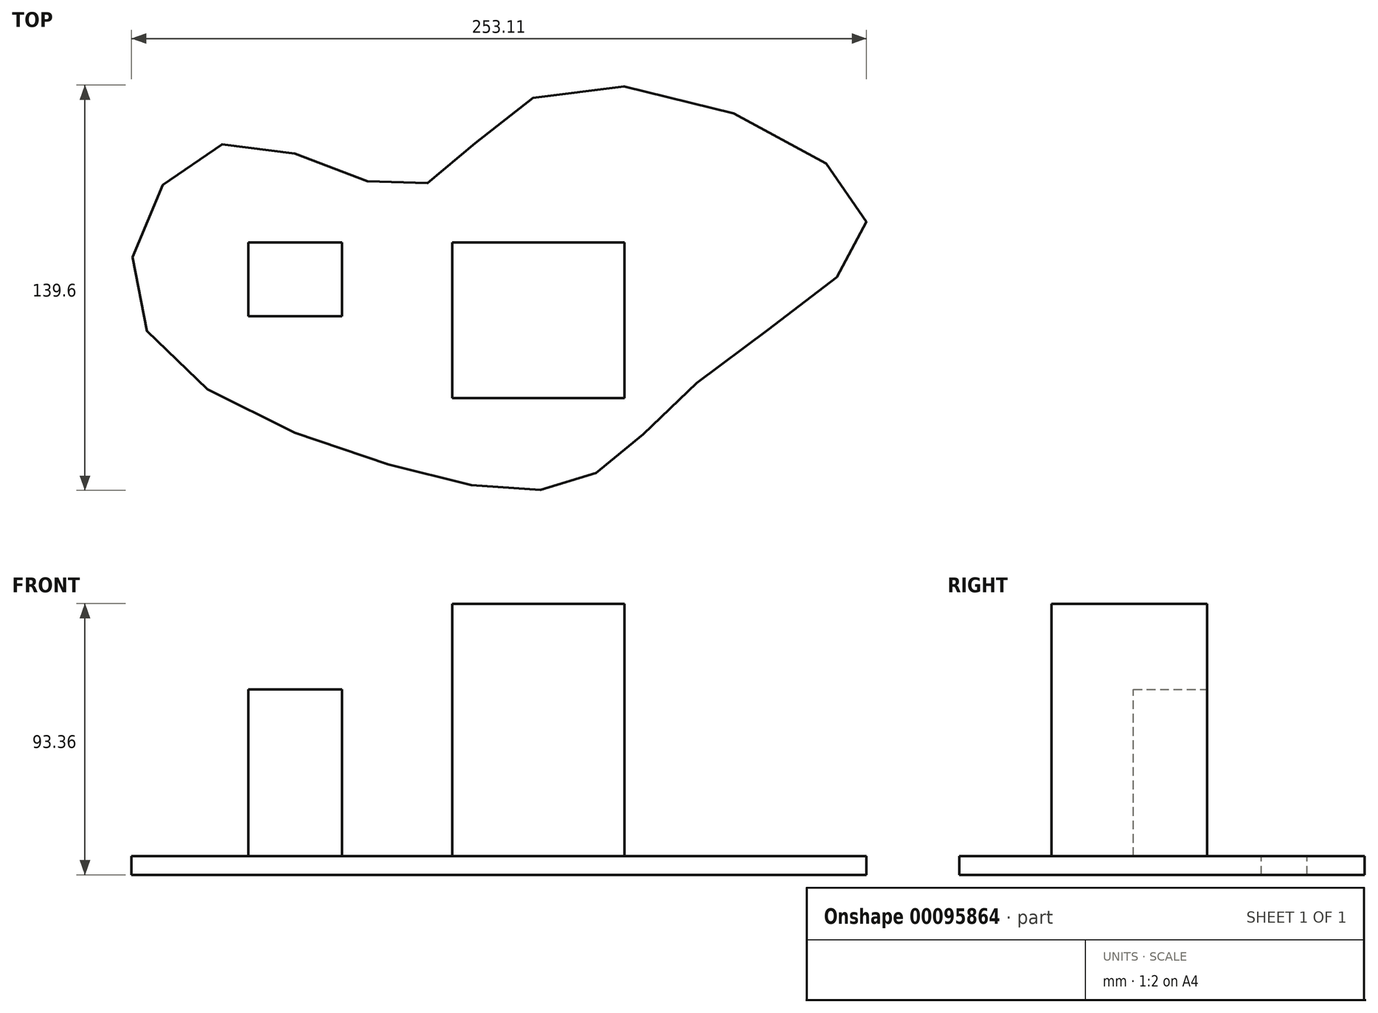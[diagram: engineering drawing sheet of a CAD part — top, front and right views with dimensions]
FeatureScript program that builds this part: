
annotation { "Feature Type Name" : "Feature", "Feature Type Description" : "" }
export const myFeature = defineFeature(function(context is Context, id is Id, definition is map)
    precondition{}
    {
        {
            var Q0;
            Q0=qCreatedBy(makeId("Front.planeOp"),FACE);
            var sketch = newSketch(context, id + "F0", { "sketchPlane" : qUnion([Q0])});
            skLineSegment(sketch, "E0.bottom", {"start": v(0, 0) * mm, "end": v(59.24, 0) * mm});
            skLineSegment(sketch, "E0.top", {"start": v(0, 86.9) * mm, "end": v(59.24, 86.9) * mm});
            skLineSegment(sketch, "E0.left", {"start": v(0, 0) * mm, "end": v(0, 86.9) * mm});
            skLineSegment(sketch, "E0.right", {"start": v(59.24, 0) * mm, "end": v(59.24, 86.9) * mm});
            skSolve(sketch);
        }
        {
            var Q0;
            Q0=makeQuery(id+"F0.imprint","IMPRINT",FACE,{"disambiguationData":[TD([[makeQuery(id+"F0.imprint","IMPRINT",EDGE,{"derivedFrom":sQuery(id+"F0.wireOp",EDGE,"E0.bottom")}),1.0]])]});
            extrude(context, id + "F1", {"entities" : qUnion([Q0]), "depth" : 53.6 * mm});
        }
        {
            var Q0;
            Q0=qCreatedBy(makeId("Front.planeOp"),FACE);
            var sketch = newSketch(context, id + "F2", { "sketchPlane" : qUnion([Q0])});
            skLineSegment(sketch, "E1.bottom", {"start": v(-37.98, 0) * mm, "end": v(-70.25, 0) * mm});
            skLineSegment(sketch, "E1.top", {"start": v(-37.98, 57.37) * mm, "end": v(-70.25, 57.37) * mm});
            skLineSegment(sketch, "E1.left", {"start": v(-37.98, 0) * mm, "end": v(-37.98, 57.37) * mm});
            skLineSegment(sketch, "E1.right", {"start": v(-70.25, 0) * mm, "end": v(-70.25, 57.37) * mm});
            skSolve(sketch);
        }
        {
            var Q0;
            Q0=makeQuery(id+"F2.imprint","IMPRINT",FACE,{"disambiguationData":[TD([[makeQuery(id+"F2.imprint","IMPRINT",EDGE,{"derivedFrom":sQuery(id+"F2.wireOp",EDGE,"E1.bottom")}),-1.0]])]});
            extrude(context, id + "F3", {"entities" : qUnion([Q0]), "depth" : 25.4 * mm});
        }
        {
            var Q0;
            Q0=makeQuery(id+"F1.opExtrude","SWEPT_FACE",FACE,{"disambiguationData":[OSD([sQuery(id+"F0.wireOp",EDGE,"E0.bottom")])]});
            var sketch = newSketch(context, id + "F4", { "sketchPlane" : qUnion([Q0])});
            skLineSegment(sketch, "E2.0.0", {"start": v(0, 0) * mm, "end": v(59.24, 0) * mm});
            skLineSegment(sketch, "E2.0.1", {"start": v(59.24, 0) * mm, "end": v(59.24, 53.59) * mm});
            skLineSegment(sketch, "E2.0.2", {"start": v(59.24, 53.59) * mm, "end": v(0, 53.59) * mm});
            skLineSegment(sketch, "E2.0.3", {"start": v(0, 53.59) * mm, "end": v(0, 0) * mm});
            skLineSegment(sketch, "E3.0.0", {"start": v(-70.25, 0) * mm, "end": v(-37.98, 0) * mm});
            skLineSegment(sketch, "E3.0.1", {"start": v(-37.98, 0) * mm, "end": v(-37.98, 25.4) * mm});
            skLineSegment(sketch, "E3.0.2", {"start": v(-37.98, 25.4) * mm, "end": v(-70.25, 25.4) * mm});
            skLineSegment(sketch, "E3.0.3", {"start": v(-70.25, 25.4) * mm, "end": v(-70.25, 0) * mm});
            skFitSpline(sketch, "E4", {"points": [v(-21.97, 76.37) * mm, v(44.35, 81.9) * mm, v(90.77, 42.94) * mm, v(142.17, -10.12) * mm, v(35.78, -52.67) * mm, v(-13.4, -18.96) * mm, v(-79.17, -33.88) * mm, v(-109.01, 21.66) * mm, v(-21.97, 76.37) * mm]});
            skSolve(sketch);
        }
        {
            var Q0;
            Q0=makeQuery(id+"F4.imprint","IMPRINT",FACE,{"disambiguationData":[TD([[makeQuery(id+"F4.imprint","IMPRINT",EDGE,{"derivedFrom":sQuery(id+"F4.wireOp",EDGE,"E2.0.0")}),-1.0]])]});
            var Q1;
            Q1=makeQuery(id+"F4.imprint","IMPRINT",FACE,{"disambiguationData":[TD([[makeQuery(id+"F4.imprint","IMPRINT",EDGE,{"derivedFrom":sQuery(id+"F4.wireOp",EDGE,"E2.0.0")}),1.0]])]});
            var Q2;
            Q2=makeQuery(id+"F4.imprint","IMPRINT",FACE,{"disambiguationData":[TD([[makeQuery(id+"F4.imprint","IMPRINT",EDGE,{"derivedFrom":sQuery(id+"F4.wireOp",EDGE,"E3.0.0")}),1.0]])]});
            extrude(context, id + "F5", {"entities" : qUnion([Q0, Q1, Q2]), "depth" : 6.46 * mm});
        }
    });
